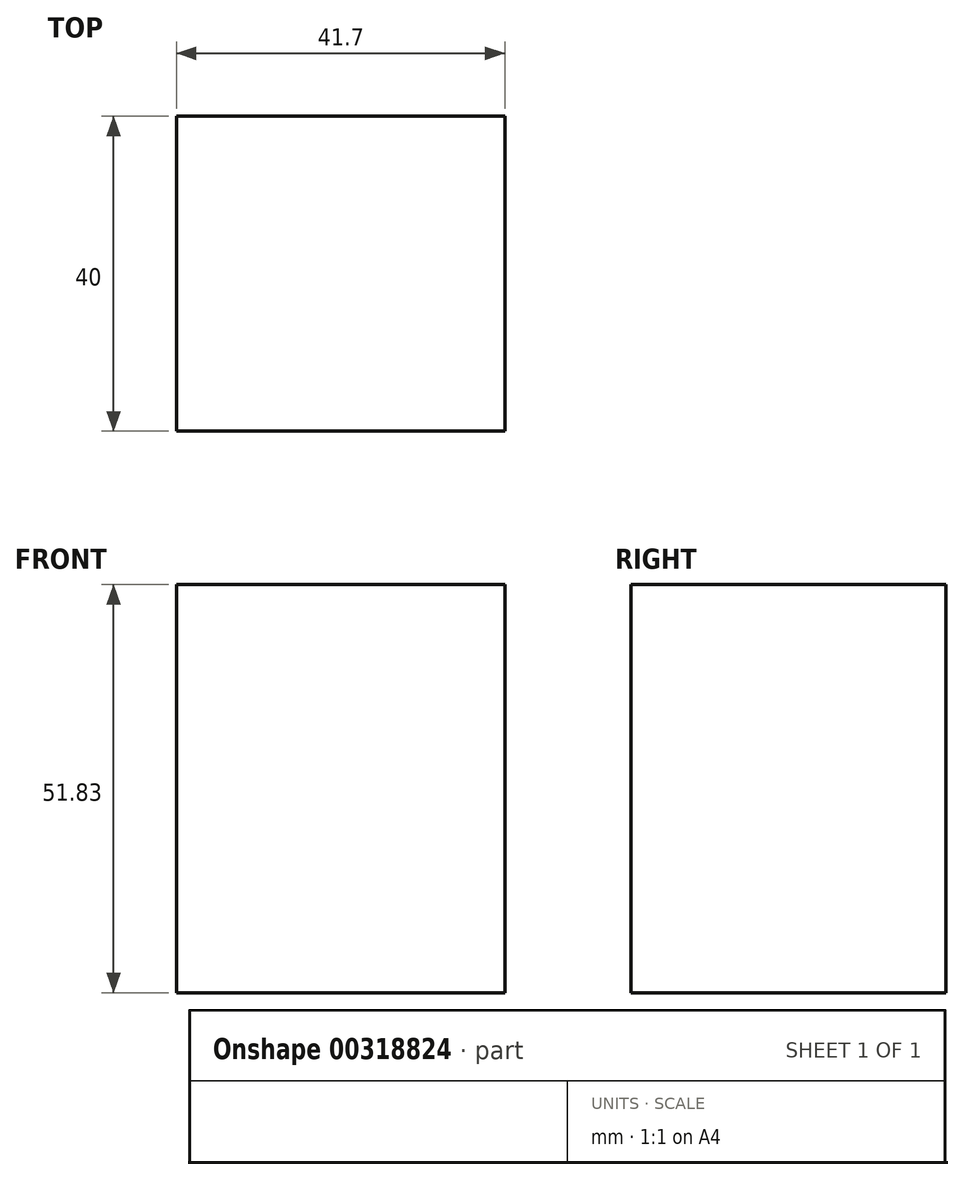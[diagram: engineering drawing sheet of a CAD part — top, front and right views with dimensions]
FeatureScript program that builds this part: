
annotation { "Feature Type Name" : "Feature", "Feature Type Description" : "" }
export const myFeature = defineFeature(function(context is Context, id is Id, definition is map)
    precondition{}
    {
        {
            var Q0;
            Q0=qCreatedBy(makeId("Front.planeOp"),FACE);
            var sketch = newSketch(context, id + "F0", { "sketchPlane" : qUnion([Q0])});
            skLineSegment(sketch, "E0.bottom", {"start": v(-32.06, 0) * mm, "end": v(9.64, 0) * mm});
            skLineSegment(sketch, "E0.top", {"start": v(-32.06, 51.83) * mm, "end": v(9.64, 51.83) * mm});
            skLineSegment(sketch, "E0.left", {"start": v(-32.06, 0) * mm, "end": v(-32.06, 51.83) * mm});
            skLineSegment(sketch, "E0.right", {"start": v(9.64, 0) * mm, "end": v(9.64, 51.83) * mm});
            skSolve(sketch);
        }
        {
            var Q0;
            Q0=makeQuery(id+"F0.imprint","IMPRINT",FACE,{"disambiguationData":[TD([[makeQuery(id+"F0.imprint","IMPRINT",EDGE,{"derivedFrom":sQuery(id+"F0.wireOp",EDGE,"E0.bottom")}),1.0]])]});
            extrude(context, id + "F1", {"entities" : qUnion([Q0]), "depth" : 60 * mm});
        }
        {
            var Q0;
            Q0=makeQuery(id+"F1.opExtrude","CAP_FACE",FACE,{"disambiguationData":[OSD([sQuery(id+"F0.wireOp",EDGE,"E0.bottom"),sQuery(id+"F0.wireOp",EDGE,"E0.top"),sQuery(id+"F0.wireOp",EDGE,"E0.left"),sQuery(id+"F0.wireOp",EDGE,"E0.right")])],"isStart":false});
            extrude(context, id + "F2", {"entities" : qUnion([Q0]), "operationType" : NewBodyOperationType.REMOVE, "oppositeDirection" : true, "depth" : 20 * mm});
        }
    });
